# Revit family: HC_Heat Pump_MEPcontent_Itho Daalderop_WPV-H 3G_NL-NL1
name_source: partatom
category: Mechanical Equipment
units: mm (PartAtom-declared; Revit-internal decimal feet)

## family parameters
Always vertical = Yes
Classification = None
Cut with Voids When Loaded = No
OmniClass Number = 23.75.10.21
OmniClass Title = Heat Pumps
Part Type = Normal
Room Calculation Point = No
Round Connector Dimension = Use Diameter
Shared = No
Work Plane-Based = No

## types (3) — shared parameters
Article Description = Warmtepomp voorraadvat horizontaal
Base Family Version = 23.10
Black = Color RGB 050-050-050
Content Supplier URL = www.MEPcontent.com
Custom = No
Depth = 600 mm
Description = Warmtepomp voorraadvat horizontaal
Domestic Cold Water Diameter = 22 mm  [stored 0.0721785 ft]
Domestic Hot Water Diameter = 22 mm  [stored 0.0721785 ft]
EMCS Version = 5.0
ETIM Article Class = EC011794
Family Version = 23.10
GLN = 8712922000014
Height = 614 mm  [stored 2.01444 ft]
Hertz = 50 Hz
Hydronic Return Diameter = 22 mm  [stored 0.0721785 ft]
Hydronic Supply Diameter = 22 mm  [stored 0.0721785 ft]
IFCExportAs = IfcPump
IFCExportType = NOTDEFINED
Light Grey = Color RAL 9006
MEPcontent Class = HEATPUMP
Manufacturer = Itho Daalderop
Manufacturer URL = https://www.ithodaalderop.nl
Phase = 1
Product Line = Itho Daalderop
Revit Version = 2021
URL = https://mep.trimble.com
Voltage = 230 V
White = Color RAL 9003
zero-valued in all types: Default Elevation

## per-type parameters (varying)
| type | GTIN | Manufacturer Art. No. | Width |
| WPV-H 200L 3G | 8713418049166 | 03-00730 | 1302 mm  [stored 4.27165 ft] |
| WPV-H 240L 3G | 8713418049173 | 03-00731 | 1540 mm |
| WPV-H 270L 3G | 8713418049180 | 03-00732 | 1690 mm |

note: column(s) folded — value = type name in every type: Article Type, Model

note: [stored X ft] marks values corroborated as IEEE doubles in the binary element streams (Revit-internal decimal feet)

## geometry (parser evidence)
native form markers: Sweep x5
no freeform markers — native parametric forms only
